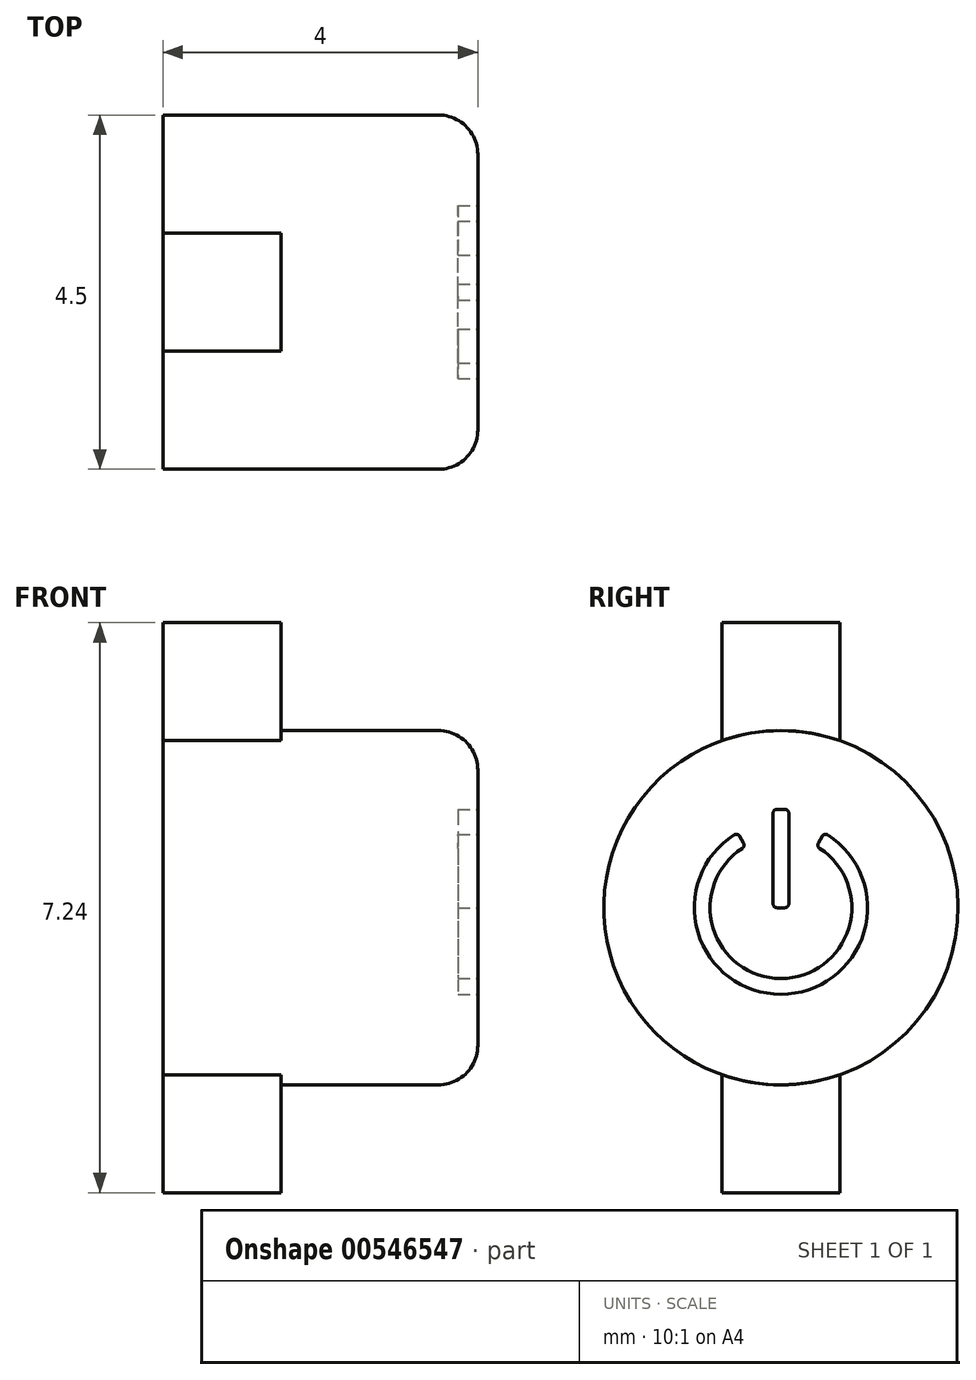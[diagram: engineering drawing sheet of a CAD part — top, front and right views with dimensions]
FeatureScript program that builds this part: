
annotation { "Feature Type Name" : "Feature", "Feature Type Description" : "" }
export const myFeature = defineFeature(function(context is Context, id is Id, definition is map)
    precondition{}
    {
        {
            var Q0;
            Q0=qCreatedBy(makeId("Right.planeOp"),FACE);
            var sketch = newSketch(context, id + "F0", { "sketchPlane" : qUnion([Q0])});
            skCircle(sketch, "E0", {"center": v(0, 0) * mm, "radius": 2.25 * mm});
            skSolve(sketch);
        }
        {
            var Q0;
            Q0=makeQuery(id+"F0.imprint","IMPRINT",FACE,{"disambiguationData":[TD([[makeQuery(id+"F0.imprint","IMPRINT",EDGE,{"derivedFrom":sQuery(id+"F0.wireOp",EDGE,"E0")}),1.0]])]});
            extrude(context, id + "F1", {"entities" : qUnion([Q0]), "endBound" : BoundingType.SYMMETRIC, "depth" : 4 * mm, "offsetDistance" : 25 * mm});
        }
        {
            var Q0;
            Q0=makeQuery(id+"F1.opExtrude","CAP_FACE",FACE,{"disambiguationData":[OSD([sQuery(id+"F0.wireOp",EDGE,"E0")])],"isStart":false});
            fillet(context, id + "F2", {"entities" : qUnion([Q0]), "radius" : 0.5 * mm, "tangentPropagation" : true, "allowEdgeOverflow" : false});
        }
        {
            var Q0;
            Q0=makeQuery(id+"F1.opExtrude","CAP_FACE",FACE,{"disambiguationData":[OSD([sQuery(id+"F0.wireOp",EDGE,"E0")])],"isStart":true});
            var sketch = newSketch(context, id + "F3", { "sketchPlane" : qUnion([Q0])});
            skArc(sketch, "E1", {"start": v(-0.77, -2.11) * mm, "mid": v(2.25, -0.01) * mm, "end": v(-0.75, 2.12) * mm});
            skLineSegment(sketch, "E2.top", {"start": v(-0.75, 3.62) * mm, "end": v(0.75, 3.62) * mm});
            skLineSegment(sketch, "E2.left", {"start": v(-0.75, 2.12) * mm, "end": v(-0.75, 3.62) * mm});
            skLineSegment(sketch, "E2.right", {"start": v(0.75, 2.12) * mm, "end": v(0.75, 3.62) * mm});
            skPoint(sketch, "E2.middle", {"position": v(0, 3.06) * mm});
            skPoint(sketch, "E3.orphan", {"position": v(-0.75, 2.5) * mm});
            skPoint(sketch, "E4.orphan", {"position": v(0.75, 2.5) * mm});
            skLineSegment(sketch, "E5.MirrorCS", {"start": v(0.75, -2.12) * mm, "end": v(0.75, -3.62) * mm});
            skLineSegment(sketch, "E6.MirrorCS", {"start": v(-0.75, -2.12) * mm, "end": v(-0.75, -3.62) * mm});
            skLineSegment(sketch, "E7.MirrorCS", {"start": v(-0.75, -3.62) * mm, "end": v(0.75, -3.62) * mm});
            skPoint(sketch, "E8.MirrorP", {"position": v(-0.75, -2.5) * mm});
            skPoint(sketch, "E9.MirrorP", {"position": v(0, -3.06) * mm});
            skPoint(sketch, "E10.MirrorP", {"position": v(0.75, -2.5) * mm});
            skSolve(sketch);
        }
        {
            var Q0;
            Q0=qSketchRegion(id+"F3",true);
            extrude(context, id + "F4", {"entities" : qUnion([Q0]), "operationType" : NewBodyOperationType.ADD, "oppositeDirection" : true, "depth" : 1.5 * mm, "offsetDistance" : 25 * mm});
        }
        {
            var Q0;
            Q0=makeQuery(id+"F1.opExtrude","CAP_FACE",FACE,{"disambiguationData":[OSD([sQuery(id+"F0.wireOp",EDGE,"E0")])],"isStart":false});
            var sketch = newSketch(context, id + "F5", { "sketchPlane" : qUnion([Q0])});
            skLineSegment(sketch, "E11.bottom", {"start": v(-0.05, 1.25) * mm, "end": v(0.05, 1.25) * mm});
            skLineSegment(sketch, "E11.left", {"start": v(-0.1, 1.2) * mm, "end": v(-0.1, 0.05) * mm});
            skLineSegment(sketch, "E11.right", {"start": v(0.1, 1.2) * mm, "end": v(0.1, 0.05) * mm});
            skPoint(sketch, "E11.middle", {"position": v(0, 0) * mm});
            skLineSegment(sketch, "E12", {"start": v(-0.05, 0) * mm, "end": v(0.05, 0) * mm});
            skPoint(sketch, "E13.orphan", {"position": v(-0.1, -1.25) * mm});
            skPoint(sketch, "E14.orphan", {"position": v(0.1, -1.25) * mm});
            skArc(sketch, "E15.0", {"start": v(-0.5, 0.75) * mm, "mid": v(0, -0.9) * mm, "end": v(0.5, 0.75) * mm});
            skArc(sketch, "E16.0", {"start": v(-0.6, 0.93) * mm, "mid": v(0, -1.1) * mm, "end": v(0.6, 0.93) * mm});
            skLineSegment(sketch, "E17", {"start": v(-0.52, 0.9) * mm, "end": v(-0.47, 0.82) * mm});
            skLineSegment(sketch, "E18.trimOffspring", {"start": v(0.47, 0.82) * mm, "end": v(0.52, 0.9) * mm});
            skPoint(sketch, "E19.visualSharp", {"position": v(-0.1, 1.25) * mm});
            skArc(sketch, "E19.filletArc", {"start": v(-0.05, 1.25) * mm, "mid": v(-0.09, 1.24) * mm, "end": v(-0.1, 1.2) * mm});
            skPoint(sketch, "E20.visualSharp", {"position": v(0.1, 1.25) * mm});
            skArc(sketch, "E20.filletArc", {"start": v(0.1, 1.2) * mm, "mid": v(0.09, 1.24) * mm, "end": v(0.05, 1.25) * mm});
            skPoint(sketch, "E21.visualSharp", {"position": v(-0.1, 0) * mm});
            skArc(sketch, "E21.filletArc", {"start": v(-0.1, 0.05) * mm, "mid": v(-0.09, 0.01) * mm, "end": v(-0.05, 0) * mm});
            skPoint(sketch, "E22.visualSharp", {"position": v(0.1, 0) * mm});
            skArc(sketch, "E22.filletArc", {"start": v(0.05, 0) * mm, "mid": v(0.09, 0.01) * mm, "end": v(0.1, 0.05) * mm});
            skPoint(sketch, "E23.visualSharp", {"position": v(-0.45, 0.78) * mm});
            skArc(sketch, "E23.filletArc", {"start": v(-0.5, 0.75) * mm, "mid": v(-0.47, 0.78) * mm, "end": v(-0.47, 0.82) * mm});
            skPoint(sketch, "E24.visualSharp", {"position": v(-0.55, 0.95) * mm});
            skArc(sketch, "E24.filletArc", {"start": v(-0.52, 0.9) * mm, "mid": v(-0.56, 0.93) * mm, "end": v(-0.6, 0.93) * mm});
            skPoint(sketch, "E25.visualSharp", {"position": v(0.45, 0.78) * mm});
            skArc(sketch, "E25.filletArc", {"start": v(0.47, 0.82) * mm, "mid": v(0.47, 0.78) * mm, "end": v(0.5, 0.75) * mm});
            skPoint(sketch, "E26.visualSharp", {"position": v(0.55, 0.95) * mm});
            skArc(sketch, "E26.filletArc", {"start": v(0.6, 0.93) * mm, "mid": v(0.56, 0.93) * mm, "end": v(0.52, 0.9) * mm});
            skSolve(sketch);
        }
        {
            var Q0;
            Q0=qSketchRegion(id+"F5",true);
            extrude(context, id + "F6", {"entities" : qUnion([Q0]), "operationType" : NewBodyOperationType.REMOVE, "oppositeDirection" : true, "depth" : .25 * mm, "offsetDistance" : 25 * mm});
        }
    });
